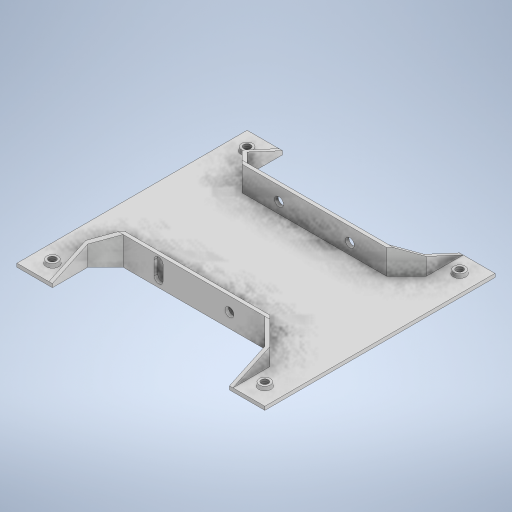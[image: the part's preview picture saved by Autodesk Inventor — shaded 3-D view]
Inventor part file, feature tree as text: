
AUTODESK INVENTOR PART (.ipt)
format: ipt  version: 2023 (Build 270158030, 158C)  size: 415,744 bytes
history: native  units: in
note: dims shown in document units (in); Inventor stores cm internally (conversion verified against a paired STEP export)
features: sketch x7, extrude x6, hole x1, pattern_linear x1, projected_geometry x1
ambient origin geometry x8: Origin, YZ Plane, XZ Plane, XY Plane, X Axis, Y Axis, Z Axis, Center Point
bodies: Solid1 (feature_tree)
feature tree (16):
  extrude  "Extrusion1"  Depth=7.0in
  extrude  "Extrusion2"  Depth=1.0in
  extrude  "Extrusion3"  Depth=1.0in
  extrude  "Extrusion4"  Depth=1.0in
  hole  "Hole1"  [1 undecoded]
  pattern_linear  "Rectangular Pattern1"  Spacing1=135.0deg  [1 undecoded]
  extrude  "Extrusion5"  Depth=0.1in TaperAngle=0.0deg
  extrude  "Extrusion6"  Depth=0.1in
  sketch  "Sketch1"  dims[d1=6.5in d2=7.0in]
  sketch  "Sketch2"  dims[d3=1.0in d4=1.0in]
  projected_geometry  "Projected Loop1"
  sketch  "Sketch3"  dims[d6=1.0in d7=1.0in]
  sketch  "Sketch4"  dims[d10=1.0in d11=1.0in]
  sketch  "Sketch5"  dims[d12=1.0in d13=1.0in]
  sketch  "Sketch6"  dims[d16=4.0in]
  sketch  "Sketch7"  dims[d17=135.0deg d18=135.0deg d19=0.1in d20=0.0in d21=0.1in d22=0.7in d23=0.0in d24=0.7in d25=5.2in d26=0.0in d27=1.0in d28=1.0in d29=0.35in d30=0.1in d31=-0.0687in d32=0.3147in d33=0.3147in d34=0.196in d35=0.5in d36=0.375in d37=0.25in d38=0.5635in d39=1.0in d40=0.8108in d42=0.7874in d44=5.5in d45=0.7874in d47=6.0in d48=4.0in d49=0.1554in d51=1.0in d52=1.0in d53=0.25in d54=0.25in d55=3.5in d56=0.0in d57=0.175in d58=0.25in d60=0.25in d61=0.25in d62=0.225in d63=0.1in d64=0.125in d65=0.525in d66=0.1in d67=0.0in]
note: 2 required parameter values undecoded (feature->parameter linkage not recoverable at this tier; creation-order binding heuristic only, values carry confidence <= 0.55)
